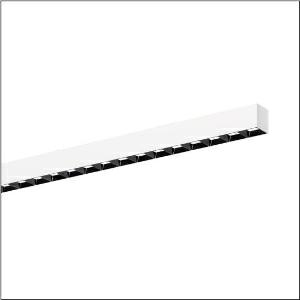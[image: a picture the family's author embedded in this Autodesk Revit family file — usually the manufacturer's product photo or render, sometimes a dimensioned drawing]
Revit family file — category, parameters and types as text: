
# Revit family: silica_r__21_51mx21da34wb_4769
name_source: partatom
category: Lighting Fixtures
units: mm (PartAtom-declared; Revit-internal decimal feet)

## family parameters
Cut with Voids When Loaded = No
Host = Face
Light Source = No
Part Type = Normal
Room Calculation Point = No
Round Connector Dimension = Use Diameter
Shared = No

## types (1)
- --- (1 x LED, 4320 lm, 27.4 W, 3000K)
    Apparent Load = 27 VA
    CIE Flux Codes = 87 99 100 100 100
    Color Rendering = 80
    Color Temperature = 3000K
    Default Elevation = 1800 mm
    Description = Silica® 21, office luminaire, primary light control with darklight reflector, of PMMA, black, CAT 2 (L<= 3000cd/m²), light emission: direct distribution, primary light characteristic: symmetric, installation type: surface-mounted, LED, rated luminous flux: 4.320lm, luminous efficacy: 158lm/W, light colour: 830, colour temperature: 3000K, with terminal, 3+2-pole, max. 2.5mm², mains connection: 220..240V, AC, 50/60Hz, rated input power: 27.4W, luminaire housing, of aluminium, traffic white (RAL 9016), length: 1.204mm, width: 53mm, height: 53mm, protection rating (complete): IP20, insulation class (complete): insulation class I (protective earthing), certification: CE, permissible operating ambient temperature: 0..+35°C, standard: EN 50419, packaging unit: 1 piece
    Height = 0 mm  [stored 0 ft]
    Lamp = 1 x LED
    Lamp Light Flux = 4320 lm
    Lamp Power = 27.4 W
    Lamp count = 1
    Length = 1204 mm
    Luminous efficacy = 158 lm/W
    Manufacturer = Siteco
    ModVariant = No
    Model = 51MX21DA34WB
    Mounting Place = Ceiling
    Mounting Type = Recessed
    Number of Poles = 1
    OnlyDefault = Yes
    Power Factor = 1
    Product Name = Silica® 21
    Product group = office luminaire | ceiling recessed
    ProductGroupID = 400
    Protection Class = Protection class I
    Protection Degree = IP 20
    RLX_Detail_Level = 1
    RLX_Emergency_Light_Flux = 0 lm
    RLX_Emergency_Type = 0
    RLX_Emergency_Type_DB = No
    RlxData = <blob elided: 41001 chars, md5=047434d5>
    Socket = socket
    Standby Power = 0 W
    System Light Flux = 4320 lm
    System Power = 27 W
    Type Comments = factory setting: luminous flux: 100 % | dim-lin: 254 | 393 mA
    Type Image = l_1335873.jpg
    URL = http://relux.com
    VarID = @adj_093755
    Voltage = 0 V
    Weight = 0.00 kg
    Width = 53 mm

note: [stored X ft] marks values corroborated as IEEE doubles in the binary element streams (Revit-internal decimal feet)

## geometry (parser evidence)
native form markers: Blend x4, Sweep x11
no freeform markers — native parametric forms only
